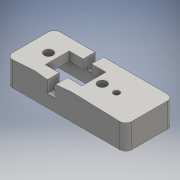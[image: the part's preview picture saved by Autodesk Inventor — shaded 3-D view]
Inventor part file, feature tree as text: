
AUTODESK INVENTOR PART (.ipt)
format: ipt  version: 2016 SP1 (Build 200210100, 210)  size: 194,560 bytes
history: native  units: mm
features: sketch x5, extrude x5, reference x2, plane x1
ambient origin geometry x8: Origin, YZ Plane, XZ Plane, XY Plane, X Axis, Y Axis, Z Axis, Center Point
bodies: Solid1 (feature_tree)
feature tree (13):
  plane  "Work Plane1"
  sketch  "Sketch1"  dims[d2=6.0mm d3=12.684184mm]
  extrude  "Extrusion4"  Depth=12.684184mm
  extrude  "Extrusion5"  Depth=2.0mm
  extrude  "Extrusion6"  Depth=5.2mm
  extrude  "Extrusion7"  Depth=3.0mm TaperAngle=0.0deg
  extrude  "Extrusion8"  Depth=4.0mm
  sketch  "Sketch5"  dims[d4=2.0mm d5=7.0mm]
  reference  "Reference11"
  reference  "Reference12"
  sketch  "Sketch6"  dims[d14=5.2mm d15=0.0mm d16=6.0mm]
  sketch  "Sketch7"  dims[d17=7.0mm d18=3.0mm d19=0.0mm]
  sketch  "Sketch8"  dims[d20=4.0mm d21=0.0mm d22=4.0mm d23=4.0mm d24=0.5mm d25=5.2mm d26=0.0mm d27=2.0mm d28=5.0mm d29=4.0mm d30=0.0mm d31=1.0mm]
